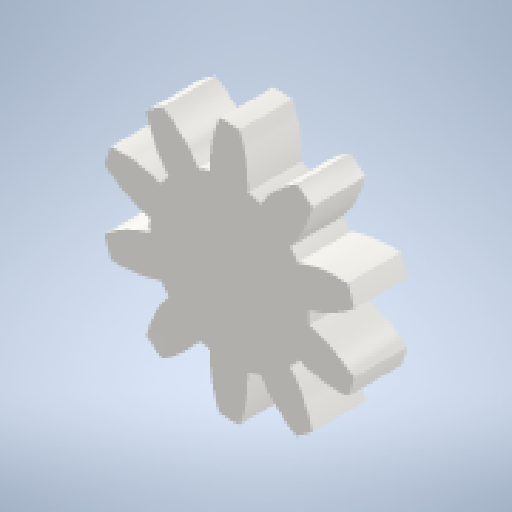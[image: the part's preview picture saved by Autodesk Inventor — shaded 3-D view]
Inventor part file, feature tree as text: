
AUTODESK INVENTOR PART (.ipt)
format: ipt  version: 2024 (Build 280153000, 153)  size: 216,576 bytes
history: native  units: mm (DEFAULTED — no unit token found)
features: plane x3, other x3, extrude x1, sketch x1
ambient origin geometry x8: Origin, YZ Plane, XZ Plane, XY Plane, X Axis, Y Axis, Z Axis, Center Point
bodies: Solid1 (feature_tree)
feature tree (8):
  extrude  "Extrusion1"  Depth=20.0mm TaperAngle=0.0deg
  plane  "Work Plane2"
  plane  "Work Plane8"
  plane  "Work Plane9"
  other  "Spur Gear"
  sketch  "Sketch1"  dims[d0=24.0mm d1=20.0mm d2=0.0mm d3=20.0mm d4=10.0mm d5=0.0mm d16=36.0mm d17=0.0mm d34=3.141593mm d39=0.0mm d41=0.0mm d43=36.0mm d46=36.0mm d47=0.0mm d48=0.0mm d49=0.5mm d50=0.872665mm d51=0.5mm d52=0.872665mm]
  other  "Srf1"
  other  "Pitch Diameter"
